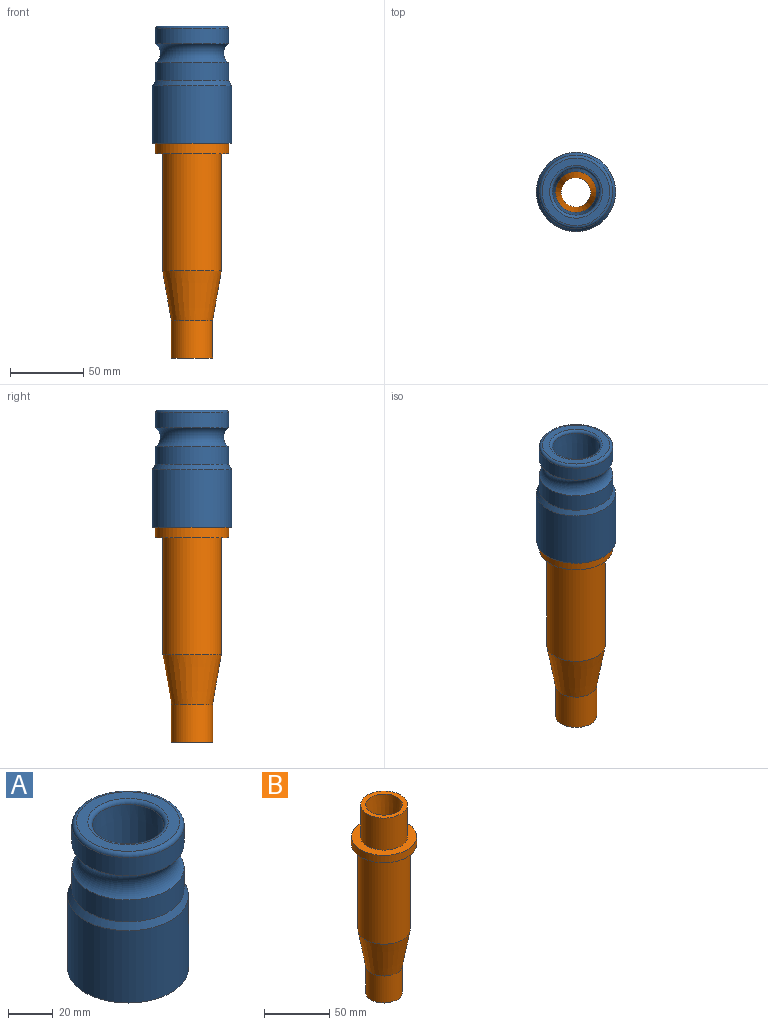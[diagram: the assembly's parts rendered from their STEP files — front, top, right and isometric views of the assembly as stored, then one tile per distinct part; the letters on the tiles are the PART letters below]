
ASSEMBLY  parts=2 mates=1
PART A: 12 faces, bbox 64.1x64.1x80 mm
  f0: cone r=16mm half-angle=2.3deg, axis (0,0,1), area 4523.4mm2, adj f8,f11
  f1: plane 46x46mm, normal (0,0,1), area 652.9mm2, adj f8,f9
  f2: cylinder r=25mm len=50mm, axis (0,0,1), area 1570.8mm2, adj f3,f9
  f3: torus R=29.59mm, axis (0,0,1), area 2195.2mm2, adj f2,f4
  f4: cylinder r=25mm len=50mm, axis (0,0,1), area 1885mm2, adj f3,f5
  f5: cone r=25mm half-angle=30deg, axis (0,0,-1), area 653.5mm2, adj f4,f6
  f6: cylinder r=27mm len=54mm, axis (0,0,1), area 6690.2mm2, adj f5,f7
  f7: plane 54x54mm, normal (0,0,-1), area 1272.3mm2, adj f6,f10
  f8: torus R=17.92mm, axis (0,0,1), area 320.6mm2, adj f0,f1
  f9: torus R=23mm, axis (0,0,1), area 479.1mm2, adj f1,f2
  f10: cylinder r=18mm len=36mm, axis (0,0,-1), area 3392.9mm2, adj f7,f11
  f11: plane 36x36mm, normal (0,0,-1), area 402.1mm2, adj f0,f10
PART B: 10 faces, bbox 50x50x176.3 mm
  f0: cylinder r=25mm len=50mm, axis (0,0,1), area 1085.6mm2, adj f1,f9
  f1: plane 50x50mm, normal (0,0,-1), area 706.9mm2, adj f0,f2
  f2: cylinder r=20mm len=80mm, axis (0,0,1), area 10053.1mm2, adj f1,f3
  f3: cone r=20mm half-angle=10deg, axis (0,0,1), area 3690.7mm2, adj f2,f4
  f4: cylinder r=14mm len=28mm, axis (0,0,1), area 2227.8mm2, adj f3,f5
  f5: plane 28x28mm, normal (0,0,-1), area 301.6mm2, adj f4,f6
  f6: cone r=10mm half-angle=1.3deg, axis (0,0,1), area 13293.4mm2, adj f5,f7
  f7: plane 36x36mm, normal (0,0,1), area 402.1mm2, adj f6,f8
  f8: cylinder r=18mm len=36mm, axis (0,0,1), area 3392.9mm2, adj f7,f9
  f9: plane 50x50mm, normal (0,0,1), area 945.6mm2, adj f0,f8
PLACE A t=(-25.38,6.67,31.89)mm
PLACE B t=(-25.38,6.67,-47.03)mm
MATE fastened B.f0 <-> A.f10  axis (0,0,1) through (-25.38,6.67,22.46)mm
